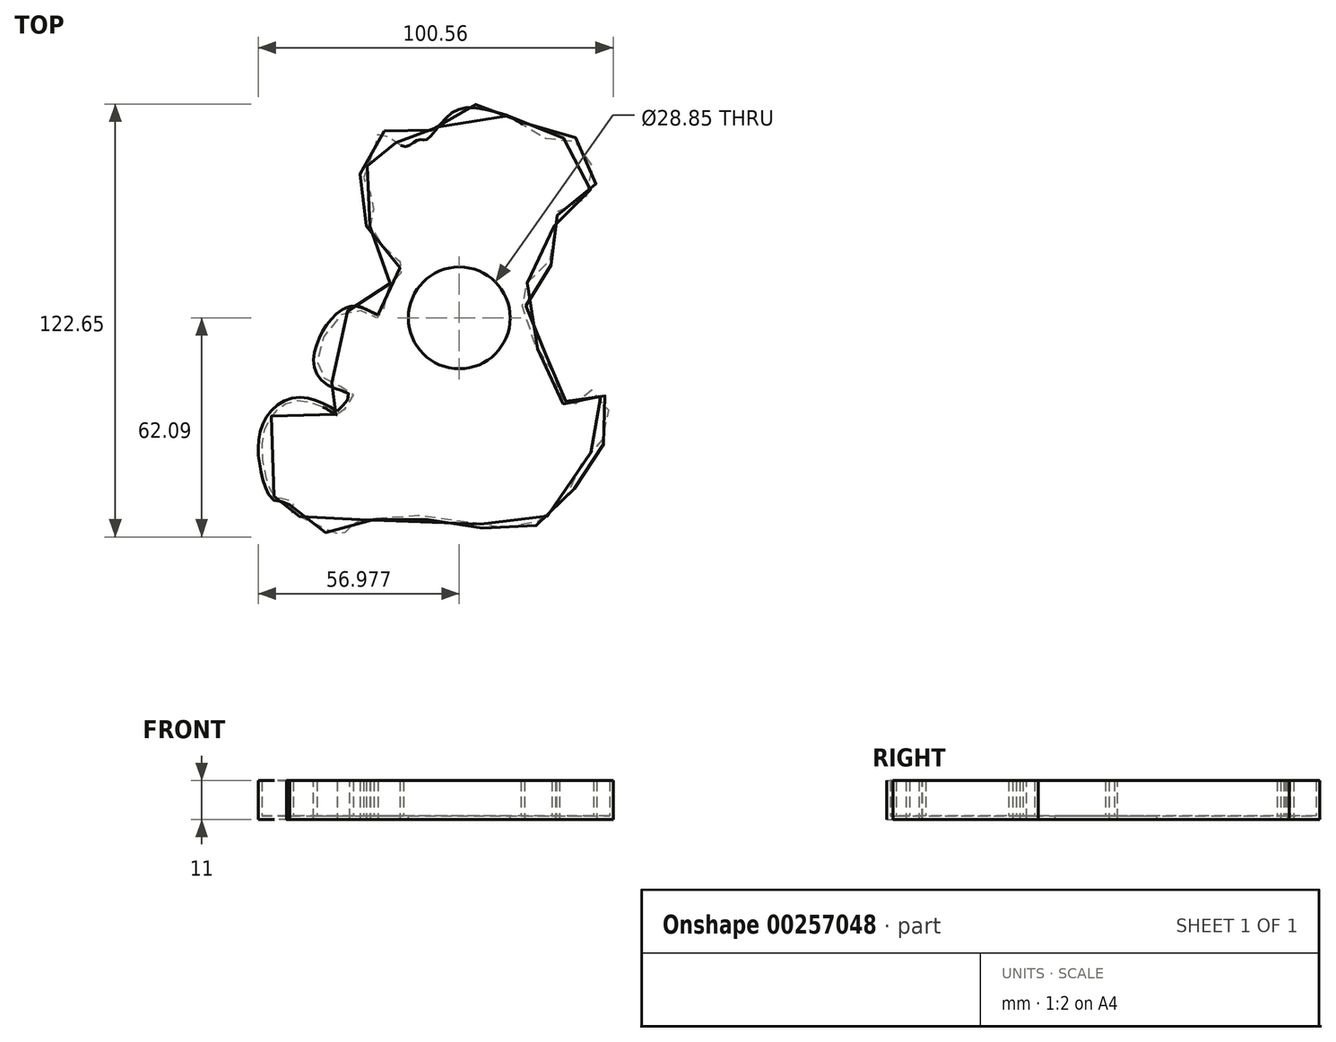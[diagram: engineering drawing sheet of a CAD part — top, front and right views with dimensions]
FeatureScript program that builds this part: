
annotation { "Feature Type Name" : "Feature", "Feature Type Description" : "" }
export const myFeature = defineFeature(function(context is Context, id is Id, definition is map)
    precondition{}
    {
        {
            var Q0;
            Q0=qCreatedBy(makeId("Top.planeOp"),FACE);
            var sketch = newSketch(context, id + "F0", { "sketchPlane" : qUnion([Q0])});
            skFitSpline(sketch, "E0", {"points": [v(-20.66, -57.11) * mm, v(10.14, -57.7) * mm, v(18.13, -59.26) * mm, v(27.3, -58.48) * mm, v(37.04, -51.85) * mm, v(42.3, -40.93) * mm, v(47.96, -34.7) * mm, v(49.9, -26.9) * mm, v(46.6, -21.44) * mm, v(42.89, -20.47) * mm, v(39.57, -25.15) * mm, v(36.84, -24.37) * mm, v(36.26, -20.27) * mm, v(32.17, -12.48) * mm, v(27.3, -4.1) * mm, v(25.15, 8.58) * mm, v(27.1, 10.14) * mm, v(33.72, 17.35) * mm, v(34.5, 25.15) * mm, v(33.92, 29.43) * mm, v(40.35, 31.38) * mm, v(45.23, 38.6) * mm, v(43.67, 46.98) * mm, v(37.43, 50.88) * mm, v(29.83, 51.07) * mm, v(24.37, 55.55) * mm, v(16.38, 58.67) * mm, v(5.65, 58.28) * mm, v(-1.95, 50.49) * mm, v(-4.1, 50.49) * mm, v(-7.8, 48.54) * mm, v(-12.67, 51.27) * mm, v(-15.8, 51.85) * mm, v(-16.96, 46.4) * mm, v(-19.69, 39.76) * mm, v(-16.76, 32.36) * mm, v(-17.54, 24.56) * mm, v(-8.38, 14.23) * mm, v(-12.28, 9.55) * mm, v(-15.2, 0) * mm, v(-22.61, 2.34) * mm, v(-32.75, -10.72) * mm, v(-28.66, -18.52) * mm, v(-22.61, -21.83) * mm, v(-26.9, -27.48) * mm, v(-27.16, -27.52) * mm, v(-27.61, -27.26) * mm, v(-36.45, -23.59) * mm, v(-45.03, -26.9) * mm, v(-48.54, -37.43) * mm, v(-44.84, -50.68) * mm, v(-42.3, -51.07) * mm, v(-39.57, -53.02) * mm, v(-40.55, -54.38) * mm, v(-35.09, -57.5) * mm, v(-25.54, -61.01) * mm, v(-20.66, -57.11) * mm]});
            skSolve(sketch);
        }
        {
            var Q0;
            Q0=makeQuery(id+"F0.imprint","IMPRINT",FACE,{"disambiguationData":[TD([[makeQuery(id+"F0.imprint","IMPRINT",EDGE,{"derivedFrom":sQuery(id+"F0.wireOp",EDGE,"E0")}),1.0]])]});
            extrude(context, id + "F1", {"entities" : qUnion([Q0]), "depth" : 10 * mm});
        }
        {
            var Q0;
            Q0=makeQuery(id+"F1.opExtrude","CAP_FACE",FACE,{"disambiguationData":[OSD([sQuery(id+"F0.wireOp",EDGE,"E0")])],"isStart":false});
            shell(context, id + "F2", {"entities" : qUnion([Q0]), "thickness" : 1 * mm, "oppositeDirection" : true});
        }
        {
            var Q0;
            Q0=makeQuery(id+"F0.imprint","IMPRINT",FACE,{"disambiguationData":[TD([[makeQuery(id+"F0.imprint","IMPRINT",EDGE,{"derivedFrom":sQuery(id+"F0.wireOp",EDGE,"E0")}),1.0]])]});
            var sketch = newSketch(context, id + "F3", { "sketchPlane" : qUnion([Q0])});
            skCircle(sketch, "E1", {"center": v(7.43, 0) * mm, "radius": 14.42 * mm});
            skSolve(sketch);
        }
        {
            var Q0;
            Q0 = qSketchRegion(id + "F3", true);
            extrude(context, id + "F4", {"entities" : qUnion([Q0]), "operationType" : NewBodyOperationType.REMOVE, "oppositeDirection" : true, "depth" : 25 * mm});
        }
    });
